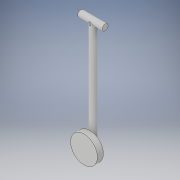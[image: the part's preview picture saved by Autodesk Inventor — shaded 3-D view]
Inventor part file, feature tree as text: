
AUTODESK INVENTOR PART (.ipt)
format: ipt  version: 2019 (Build 230136000, 136)  size: 140,288 bytes
history: native  units: in
note: dims shown in document units (in); Inventor stores cm internally (conversion verified against a paired STEP export)
features: sketch x8, extrude x4, fillet x1
ambient origin geometry x8: Origin, YZ Plane, XZ Plane, XY Plane, X Axis, Y Axis, Z Axis, Center Point
bodies: Solid1 (feature_tree)
feature tree (13):
  sketch  "Sketch1"  dims[d0=1.9685in d1=0.3937in d2=0.0in]
  extrude  "Extrusion1"  Depth=0.3937in TaperAngle=0.0deg
  extrude  "Extrusion2"  Depth=0.7874in TaperAngle=0.0deg
  extrude  "Extrusion3"  Depth=0.7874in TaperAngle=0.0deg
  sketch  "Sketch5"
  sketch  "Sketch6"
  sketch  "Sketch7"
  extrude  "Extrusion4"  [1 undecoded]
  fillet  "Fillet1"  [1 undecoded]
  sketch  "Sketch2"  dims[d3=3.5433in d4=0.7874in d5=0.0in]
  sketch  "Sketch3"  dims[d6=13.7795in d7=0.0in d8=0.7874in d9=0.0in]
  sketch  "Sketch4"  dims[d10=0.3937in]
  sketch  "Sketch8"
note: 2 required parameter values undecoded (feature->parameter linkage not recoverable at this tier; creation-order binding heuristic only, values carry confidence <= 0.55)
